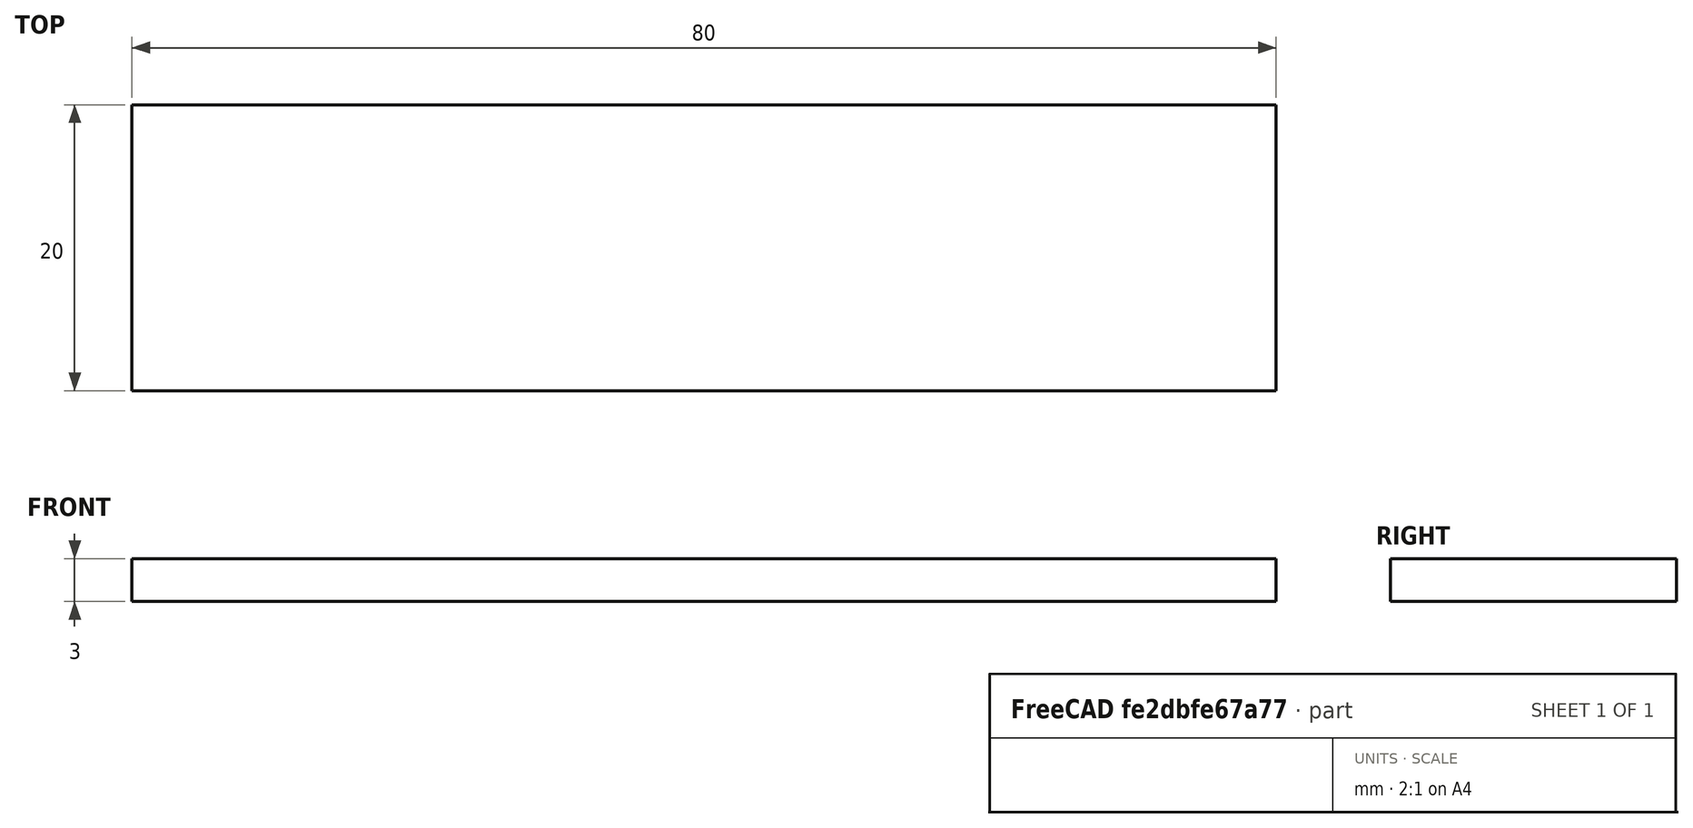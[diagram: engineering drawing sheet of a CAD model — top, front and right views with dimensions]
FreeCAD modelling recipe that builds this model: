
FCSTD DOCUMENT  (FreeCAD 0.21R33771 (Git))
Label: Grabber
License: All rights reserved
LicenseURL: http://en.wikipedia.org/wiki/All_rights_reserved
objects: Sketcher::SketchObject×3, App::DocumentObjectGroupPython×1, PartDesign::Pad×1, PartDesign::Body×1
note: 6 computed .brp shape members not serialized (recipe doc carries the construction recipe); baked Part::Feature solids carry a one-line shape summary decoded from their .brp

FEATURE [App::DocumentObjectGroupPython] ExplodedAssembly  # scripted group (container) (typed FeaturePython)
  AnimationStep = 0
  CurrentTrajectory = 0
  InAnimation = false
  RemoveAllTrajectories = false
  ResetAnimation = false
FEATURE [Sketcher::SketchObject] Sketch  label="BaseSketch"
  FullyConstrained = true
  MapMode = 5
  Support = -> [XY_Plane]
  sketch-geometry (4):
    g0: LineSegment StartX=-40 StartY=20 StartZ=0 EndX=40 EndY=20 EndZ=0
    g1: LineSegment StartX=40 StartY=20 StartZ=0 EndX=40 EndY=0 EndZ=0
    g2: LineSegment StartX=40 StartY=0 StartZ=0 EndX=-40 EndY=0 EndZ=0
    g3: LineSegment StartX=-40 StartY=0 StartZ=0 EndX=-40 EndY=20 EndZ=0
  constraints (10):
    c: Coincident(g0,g1)
    c: Coincident(g1,g2)
    c: Coincident(g2,g3)
    c: Coincident(g3,g0)
    c: Vertical(g1)
    c: Vertical(g3)
    c: Tangent(g-1,g2)
    c: Symmetric(g0,g0,g-2)
    c: DistanceY(g1,g1) = 20
    c: DistanceX(g2,g2) = 80
FEATURE [PartDesign::Pad] Pad
  Direction = (0,0,1)
  Length = 3
  Length2 = 10
  Profile = -> Sketch
  ReferenceAxis = -> Sketch [N_Axis]
  Type = 0
FEATURE [Sketcher::SketchObject] Sketch001  label="ServoTopMasterSketch"
  ExternalGeometry = -> [Pad]
  FullyConstrained = false
  MapMode = 5
  Support = -> [XY_Plane]
  sketch-geometry (25):
    g0: LineSegment StartX=4.23467 StartY=16 StartZ=0 EndX=32.2347 EndY=16 EndZ=0
    g1: LineSegment StartX=32.2347 StartY=4 StartZ=0 EndX=4.23467 EndY=4 EndZ=0
    g2: Circle CenterX=12.8347 CenterY=10 CenterZ=0 NormalX=0 NormalY=0 NormalZ=1 AngleXU=0 Radius=6.05
    g3: LineSegment StartX=40 StartY=10 StartZ=0 EndX=-40 EndY=10 EndZ=0
    g4: Circle CenterX=-12.8347 CenterY=10 CenterZ=0 NormalX=0 NormalY=0 NormalZ=1 AngleXU=0 Radius=1.5
    g5: LineSegment StartX=1.98467 StartY=16 StartZ=0 EndX=4.23467 EndY=16 EndZ=0
    g6: LineSegment StartX=4.23467 StartY=16 StartZ=0 EndX=4.23467 EndY=4 EndZ=0
    g7: LineSegment StartX=4.23467 StartY=4 StartZ=0 EndX=1.98467 EndY=4 EndZ=0
    g8: LineSegment StartX=1.98467 StartY=4 StartZ=0 EndX=1.98467 EndY=16 EndZ=0
    g9: LineSegment StartX=32.2347 StartY=16 StartZ=0 EndX=34.4847 EndY=16 EndZ=0
    g10: LineSegment StartX=34.4847 StartY=16 StartZ=0 EndX=34.4847 EndY=4 EndZ=0
    g11: LineSegment StartX=34.4847 StartY=4 StartZ=0 EndX=32.2347 EndY=4 EndZ=0
    g12: LineSegment StartX=32.2347 StartY=4 StartZ=0 EndX=32.2347 EndY=16 EndZ=0
    g13: Circle CenterX=4.23467 CenterY=10 CenterZ=0 NormalX=0 NormalY=0 NormalZ=1 AngleXU=0 Radius=1
    g14: Circle CenterX=32.2347 CenterY=10 CenterZ=0 NormalX=0 NormalY=0 NormalZ=1 AngleXU=0 Radius=1
    g15: Circle CenterX=-26.7617 CenterY=10 CenterZ=0 NormalX=0 NormalY=0 NormalZ=1 AngleXU=0 Radius=1.5
    g16: Circle CenterX=26.7617 CenterY=10 CenterZ=0 NormalX=0 NormalY=0 NormalZ=1 AngleXU=0 Radius=1.5
    g17: LineSegment StartX=6.78467 StartY=16 StartZ=0 EndX=6.78467 EndY=4 EndZ=0
    g18: LineSegment StartX=29.6847 StartY=16 StartZ=0 EndX=29.6847 EndY=4 EndZ=0
    g19: LineSegment StartX=18.2347 StartY=16 StartZ=0 EndX=18.2347 EndY=4 EndZ=0
    g20: ArcOfCircle CenterX=19.8847 CenterY=10 CenterZ=0 NormalX=0 NormalY=0 NormalZ=1 AngleXU=0 Radius=2.8 StartAngle=4.71239 EndAngle=7.85398
    g21: LineSegment StartX=18.1977 StartY=7.2 StartZ=0 EndX=19.8847 EndY=7.2 EndZ=0
    g22: LineSegment StartX=19.8847 StartY=12.8 StartZ=0 EndX=18.1977 EndY=12.8 EndZ=0
    g23: LineSegment StartX=22.6847 StartY=12.8 StartZ=0 EndX=22.6847 EndY=7.2 EndZ=0
    g24: LineSegment StartX=18.8847 StartY=12.8 StartZ=0 EndX=18.8847 EndY=7.2 EndZ=0
  constraints (71):
    c: Horizontal(g0)
    c: Horizontal(g1)
    c: PointOnObject(g3,g-5)
    c: Symmetric(g-6,g-6,g3)
    c: Symmetric(g0,g1,g3)
    c: PointOnObject(g2,g3)
    c: DistanceX(g0,g0) = 28
    c: DistanceX(g1,g2) = 8.6
    c: Symmetric(g4,g2,g-2)
    c: Coincident(g5,g6)
    c: Coincident(g6,g7)
    c: Coincident(g7,g8)
    c: Coincident(g8,g5)
    c: Horizontal(g5)
    c: Horizontal(g7)
    c: Vertical(g8)
    c: Coincident(g6,g1)
    c: Coincident(g9,g10)
    c: Coincident(g10,g11)
    c: Coincident(g11,g12)
    c: Coincident(g12,g9)
    c: Horizontal(g9)
    c: Horizontal(g11)
    c: Vertical(g10)
    c: Coincident(g9,g0)
    c: Coincident(g5,g0)
    c: PointOnObject(g14,g3)
    c: Equal(g13,g14)
    c: DistanceX(g5,g9) = 32.5
    c: Equal(g9,g5)
    c: PointOnObject(g13,g3)
    c: PointOnObject(g13,g6)
    c: Vertical(g6)
    c: Vertical(g12)
    c: PointOnObject(g14,g12)
    c: DistanceY(g10,g10) = 12
    c: Coincident(g1,g11)
    c: PointOnObject(g15,g3)
    c: Symmetric(g15,g16,g-2)
    c: Equal(g15,g16)
    c: Diameter(g15) = 3
    c: Equal(g4,g15)
    c: Diameter(g14) = 2
    c: PointOnObject(g17,g0)
    c: PointOnObject(g17,g1)
    c: Vertical(g17)
    c: PointOnObject(g18,g1)
    c: Vertical(g18)
    c: PointOnObject(g19,g0)
    c: PointOnObject(g19,g1)
    c: Symmetric(g5,g9,g19)
    c: Symmetric(g18,g17,g19)
    c: DistanceX(g17,g18) = 22.9
    c: Tangent(g2,g17)
    c: Tangent(g21,g20) = -1.5708
    c: Tangent(g20,g22) = -1.5708
    c: PointOnObject(g20,g3)
    c: Vertical(g23)
    c: Tangent(g23,g20)
    c: Vertical(g24)
    c: Tangent(g24,g2)
    c: PointOnObject(g24,g22)
    c: PointOnObject(g24,g21)
    c: Horizontal(g23,g24)
    c: Horizontal(g23,g24)
    c: DistanceX(g24,g23) = 3.8
    c: DistanceY(g20,g20) = 5.6
    c: PointOnObject(g22,g2)
    c: PointOnObject(g21,g2)
    c: Horizontal(g21)
    c: Horizontal(g22)
FEATURE [Sketcher::SketchObject] Sketch002  label="ServoFrontMasterSketch"
  FullyConstrained = false
  MapMode = 5
  Placement = pos=(0,0,0) rot=(1,0,0;1.5708rad)
  Support = -> [XZ_Plane]
  sketch-geometry (29):
    g0: LineSegment StartX=-14.8825 StartY=11.15 StartZ=0 EndX=-10.0825 EndY=11.15 EndZ=0
    g1: LineSegment StartX=17.6175 StartY=11.15 StartZ=0 EndX=17.6175 EndY=8.55 EndZ=0
    g2: LineSegment StartX=17.6175 StartY=8.55 StartZ=0 EndX=12.8175 EndY=8.55 EndZ=0
    g3: LineSegment StartX=-14.8825 StartY=8.55 StartZ=0 EndX=-14.8825 EndY=11.15 EndZ=0
    g4: LineSegment StartX=12.8175 StartY=8.55 StartZ=0 EndX=12.8175 EndY=4.25 EndZ=0
    g5: LineSegment StartX=12.8175 StartY=4.25 StartZ=0 EndX=-10.0825 EndY=4.25 EndZ=0
    g6: LineSegment StartX=-10.0825 StartY=4.25 StartZ=0 EndX=-10.0825 EndY=8.55 EndZ=0
    g7: LineSegment StartX=12.8175 StartY=11.15 StartZ=0 EndX=12.8175 EndY=28.15 EndZ=0
    g8: LineSegment StartX=12.8175 StartY=28.15 StartZ=0 EndX=-10.0825 EndY=28.15 EndZ=0
    g9: LineSegment StartX=-10.0825 StartY=28.15 StartZ=0 EndX=-10.0825 EndY=11.15 EndZ=0
    g10: LineSegment StartX=-10.0825 StartY=25.85 StartZ=0 EndX=-15.0825 EndY=25.85 EndZ=0
    g11: LineSegment StartX=-15.0825 StartY=25.85 StartZ=0 EndX=-15.0825 EndY=27.15 EndZ=0
    g12: LineSegment StartX=-15.0825 StartY=27.15 StartZ=0 EndX=-10.0825 EndY=27.15 EndZ=0
    g13: LineSegment StartX=-10.0825 StartY=27.15 StartZ=0 EndX=-10.0825 EndY=25.85 EndZ=0
    g14: LineSegment StartX=-10.0825 StartY=4.25 StartZ=0 EndX=1.91754 EndY=4.25 EndZ=0
    g15: LineSegment StartX=1.91754 StartY=4.25 StartZ=0 EndX=1.91754 EndY=0 EndZ=0
    g16: LineSegment StartX=1.91754 StartY=0 StartZ=0 EndX=-10.0825 EndY=0 EndZ=0
    g17: LineSegment StartX=-10.0825 StartY=0 StartZ=0 EndX=-10.0825 EndY=4.25 EndZ=0
    g18: LineSegment StartX=-6.58246 StartY=0 StartZ=0 EndX=-1.58246 EndY=0 EndZ=0
    g19: LineSegment StartX=-1.58246 StartY=0 StartZ=0 EndX=-1.58246 EndY=-3.2 EndZ=0
    g20: LineSegment StartX=-1.58246 StartY=-3.2 StartZ=0 EndX=-6.58246 EndY=-3.2 EndZ=0
    g21: LineSegment StartX=-6.58246 StartY=-3.2 StartZ=0 EndX=-6.58246 EndY=0 EndZ=0
    g22: LineSegment StartX=1.91754 StartY=4.25 StartZ=0 EndX=5.91754 EndY=4.25 EndZ=0
    g23: LineSegment StartX=5.91754 StartY=4.25 StartZ=0 EndX=5.91754 EndY=0 EndZ=0
    g24: LineSegment StartX=5.91754 StartY=0 StartZ=0 EndX=1.91754 EndY=0 EndZ=0
    g25: LineSegment StartX=1.91754 StartY=0 StartZ=0 EndX=1.91754 EndY=4.25 EndZ=0
    g26: LineSegment StartX=-4.08246 StartY=28.15 StartZ=0 EndX=-4.08246 EndY=-3.2 EndZ=0
    g27: LineSegment StartX=12.8175 StartY=11.15 StartZ=0 EndX=17.6175 EndY=11.15 EndZ=0
    g28: LineSegment StartX=-10.0825 StartY=8.55 StartZ=0 EndX=-14.8825 EndY=8.55 EndZ=0
  constraints (77):
    c: Coincident(g27,g1)
    c: Coincident(g1,g2)
    c: Coincident(g28,g3)
    c: Coincident(g3,g0)
    c: Horizontal(g0)
    c: Horizontal(g2)
    c: Vertical(g1)
    c: Vertical(g3)
    c: Coincident(g4,g5)
    c: Coincident(g5,g6)
    c: Horizontal(g5)
    c: Vertical(g4)
    c: Vertical(g6)
    c: Coincident(g7,g8)
    c: Coincident(g8,g9)
    c: Horizontal(g8)
    c: Coincident(g10,g11)
    c: Coincident(g11,g12)
    c: Coincident(g12,g13)
    c: Coincident(g13,g10)
    c: Horizontal(g10)
    c: Horizontal(g12)
    c: Vertical(g11)
    c: Vertical(g13)
    c: PointOnObject(g10,g9)
    c: Coincident(g14,g15)
    c: Coincident(g15,g16)
    c: Coincident(g16,g17)
    c: Coincident(g17,g14)
    c: Horizontal(g14)
    c: Vertical(g15)
    c: PointOnObject(g14,g5)
    c: Coincident(g18,g19)
    c: Coincident(g19,g20)
    c: Coincident(g20,g21)
    c: Coincident(g21,g18)
    c: Horizontal(g18)
    c: Vertical(g19)
    c: Vertical(g21)
    c: PointOnObject(g18,g16)
    c: Coincident(g22,g23)
    c: Coincident(g23,g24)
    c: Coincident(g24,g25)
    c: Coincident(g25,g22)
    c: Horizontal(g22)
    c: Vertical(g23)
    c: Vertical(g25)
    c: Coincident(g22,g14)
    c: Tangent(g9,g6)
    c: Tangent(g7,g4)
    c: Tangent(g6,g17)
    c: Symmetric(g16,g15,g26)
    c: Symmetric(g20,g19,g26)
    c: DistanceX(g8,g8) = 22.9
    c: DistanceX(g0,g27) = 32.5
    c: Coincident(g28,g6)
    c: Coincident(g27,g7)
    c: Coincident(g2,g4)
    c: Coincident(g9,g0)
    c: Tangent(g27,g0)
    c: Tangent(g28,g2)
    c: Equal(g27,g0)
    c: DistanceY(g4,g7) = 23.9
    c: DistanceX(g16,g16) = 12
    c: DistanceY(g12,g8) = 1
    c: DistanceY(g11,g11) = 1.3
    c: DistanceY(g1,g1) = 2.6
    c: Tangent(g24,g16)
    c: DistanceX(g24,g24) = 4
    c: DistanceX(g20,g20) = 5
    c: PointOnObject(g26,g8)
    c: PointOnObject(g26,g20)
    c: DistanceX(g10,g10) = 5
    c: DistanceY(g6,g6) = 4.3
    c: DistanceY(g17,g17) = 4.25
    c: DistanceY(g20,g16) = 3.2
    c: Tangent(g16,g-1)
FEATURE [PartDesign::Body] Body  label="GripperTop"
  Group = -> [Sketch,Pad,Sketch001,Sketch002]
  Origin = -> Origin
  Tip = -> Pad
